# Revit family: Супремус В
name_source: partatom
category: Осветительные приборы
units: mm (PartAtom-declared; Revit-internal decimal feet)

## family parameters
Всегда вертикально = Да
Источник света = Да
На основе рабочей плоскости = Нет
Общий = Нет
При загрузке вырезать с полостями = Нет
Размер круглого соединителя = Использовать диаметр
Тип детали = Нормальный
Точка расчета площади = Нет

## types (6) — shared parameters
ADSK_URL страницы изделия = https://www.allfresco.ru
ADSK_Единица измерения = шт.
ADSK_Завод-изготовитель = ALFRESCO
ADSK_Количество фаз = 2
ADSK_Модель = Супремус-B ДТУ-121-AF
ADSK_Напряжение = 220 В
ADSK_Полная мощность = 0 В·А
ADSK_Ток = 0 А
ADSK_Энергоэффективность = 110 лм/Вт
D_фланец_отверстия = 24 мм
H_дверка = 505 мм
H_конечной точки = 1500 мм
H_фланец = 10 мм
IP Class = IP 67
L_ассеиватель = 275 мм
L_лампа = 120 мм
L_отступ до конечной точки = 1500 мм
L_отступ до центра = 1000 мм
R_фланец_скругления = 15 мм
S1_профиль = 102 мм
S1_фланец = 280 мм
S2_профиль = 202 мм
S2_фланец = 200 мм
S_дверка = 178 мм
S_лампа = 160 мм
h_дверка = 350 мм
Блок аварийного питания = Нет
Класс защиты = 1
Класс пожароопасности = F (светильники предназначены для установки непосредственно на поверхность из нормально воспламеняемых материалов)
Климатическая зона = УХЛ1
Короб_Диаметр = 20 мм
Корпус светильника = Сталь, окрашенная, темно-серая
Материал рассеивателя = Светотехнический ПК
Область использования = Парки, скверы, общественные пространства, городская инфраструктура
Полная установленная мощность = 0 В·А
Рассеиватель = Белый_Светодиод
Светофильтр = 16777215
Смещение цветовой температуры при затухании лампы = <Нет>
Таблица выбора = Таблица параметров светильников_par4_v1
Температура эксплуатации = -40 +50
Тип ИС = LED-модуль
Тип КСС = тип Г (глубокая)
Тип ПРА = -
Тип продукции = LED-светильник
Угол наклона = 90.00°
Цветоывая температура = 2700-5500
zero-valued in all types: ADSK_Количество фаз числовое, ADSK_Коэффициент мощности

## per-type parameters (varying)
| type | 2 | ADSK_Артикул | ADSK_Масса | ADSK_Масса_Текст | ADSK_Наименование | ADSK_Номинальная мощность | ADSK_Размер_Высота | ADSK_Фактическая мощность | L_общая рассеиватели | Файл фотометрической сетки |
| ДТУ121с3 Светодиодный светильник Супремус-B ДТУ-121-AF-ДТУП1211(40Вт)-4,0 | Нет | ДТУ121с3 | 83 | 83 | ДТУ121с3 Светодиодный светильник Супремус-B ДТУ-121-AF-ДТУП1211(40Вт)-4.0 | 40 Вт | 4000 мм | 39 Вт | 326 мм | DTU-121-AF Supremus B 40W 60°x130°.ies |
| ДТУ121с4 Светодиодный светильник Супремус-B ДТУ-121-AF-ДТУП1211(40Вт)+ДТУП1211(40Вт)-4,0 | Да | ДТУ121с4 | 90 | 90 | ДТУ121с4 Светодиодный светильник Супремус-B ДТУ-121-AF-ДТУП1211(40Вт)+ДТУП1211(40Вт)-4.0 | 80 Вт | 4000 мм | 78 Вт | 550 мм | DTU-121-AF Supremus B 40W 60°x130°.ies |
| ДТУ121с5 Светодиодный светильник Супремус-B ДТУ-121-AF-ДТУП1211(40Вт)-5,0 | Нет | ДТУ121с5 | 102 | 102 | ДТУ121с5 Светодиодный светильник Супремус-B ДТУ-121-AF-ДТУП1211(40Вт)-5.0 | 40 Вт | 5000 мм | 39 Вт | 326 мм | DTU-121-AF Supremus B 40W 60°x130°.ies |
| ДТУ121с6 Светодиодный светильник Супремус-B ДТУ-121-AF-ДТУП1211(40Вт)+ДТУП1211(40Вт)-5,0 | Да | ДТУ121с6 | 109 | 109 | ДТУ121с6 Светодиодный светильник Супремус-B ДТУ-121-AF-ДТУП1211(40Вт)+ДТУП1211(40Вт)-5.0 | 80 Вт | 5000 мм | 78 Вт | 550 мм | DTU-121-AF Supremus B 40W 60°x130°.ies |
| ДТУ121с9 Светодиодный светильник Супремус-B ДТУ-121-AF-ДТУП1212(60Вт)-6,0 | Нет | ДТУ121с9 | 120 | 120 | ДТУ121с9 Светодиодный светильник Супремус-B ДТУ-121-AF-ДТУП1212(60Вт)-6.0 | 60 Вт | 6000 мм | 60 Вт | 326 мм | DTU-121-AF Supremus B 60W 60°x130°.ies |
| ДТУ121с10 Светодиодный светильник Супремус-B ДТУ-121-AF-ДТУП1212(60Вт)+ДТУП1212(60Вт)-6,0 | Да | ДТУ121с10 | 127 | 127 | ДТУ121с10 Светодиодный светильник Супремус-B ДТУ-121-AF-ДТУП1212(60Вт)+ДТУП1212(60Вт)-6.0 | 120 Вт | 6000 мм | 119 Вт | 550 мм | DTU-121-AF Supremus B 60W 60°x130°.ies |
